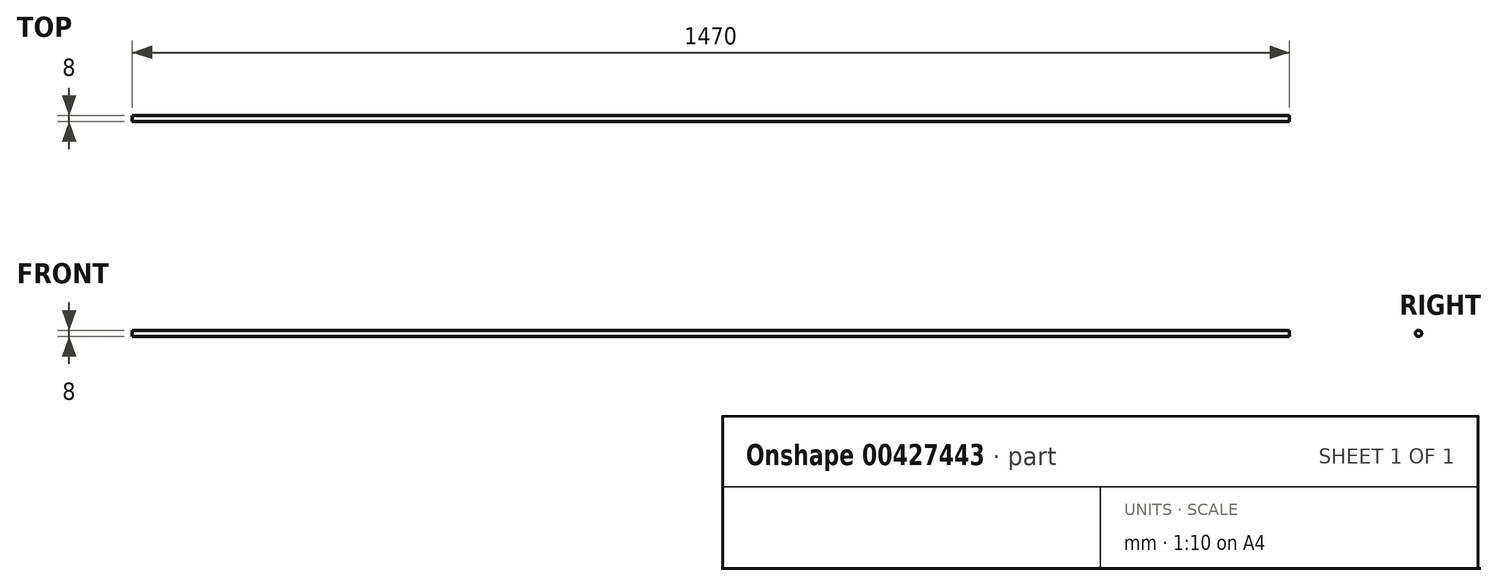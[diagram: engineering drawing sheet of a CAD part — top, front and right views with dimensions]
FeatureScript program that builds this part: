
annotation { "Feature Type Name" : "Feature", "Feature Type Description" : "" }
export const myFeature = defineFeature(function(context is Context, id is Id, definition is map)
    precondition{}
    {
        {
            var Q0;
            Q0=qCreatedBy(makeId("Right.planeOp"),FACE);
            var sketch = newSketch(context, id + "F0", { "sketchPlane" : qUnion([Q0])});
            skCircle(sketch, "E0", {"center": v(0, 0) * mm, "radius": 4 * mm});
            skSolve(sketch);
        }
        {
            var Q0;
            Q0 = qSketchRegion(id + "F0", true);
            extrude(context, id + "F1", {"entities" : qUnion([Q0]), "endBound" : BoundingType.SYMMETRIC, "depth" : 1470 * mm});
        }
    });
